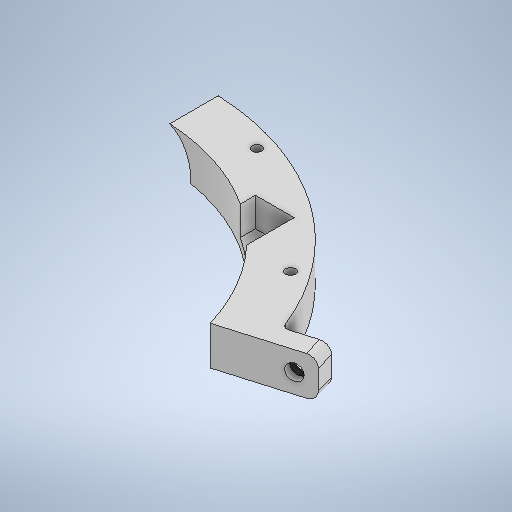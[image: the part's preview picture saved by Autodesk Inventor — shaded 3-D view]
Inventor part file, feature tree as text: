
AUTODESK INVENTOR PART (.ipt)
format: ipt  version: 2025 (Build 290162000, 162)  size: 354,816 bytes
history: native  units: in
note: dims shown in document units (in); Inventor stores cm internally (conversion verified against a paired STEP export)
features: sketch x10, extrude x7, hole x2, fillet x1, projected_geometry x1
ambient origin geometry x8: Origin, YZ Plane, XZ Plane, XY Plane, X Axis, Y Axis, Z Axis, Center Point
bodies: Solid1 (feature_tree)
feature tree (21):
  extrude  "Extrusion1"  Depth=8.6614in
  extrude  "Extrusion2"  Depth=1.4173in
  hole  "Hole1"  [1 undecoded]
  extrude  "Extrusion3"  Depth=0.1575in TaperAngle=360.0deg
  extrude  "Extrusion7"  Depth=0.1575in TaperAngle=0.0deg
  extrude  "Extrusion8"  Depth=2.7559in
  extrude  "Extrusion9"  Depth=0.7874in
  extrude  "Extrusion10"  TaperAngle=0.0deg  [1 undecoded]
  fillet  "Fillet1"  [1 undecoded]
  hole  "Hole2"  [1 undecoded]
  sketch  "Sketch1"  dims[d0=10.6299in d1=8.6614in]
  sketch  "Sketch2"  dims[d5=0.0in d6=0.0in d7=10.0394in]
  sketch  "Sketch3"  dims[d8=0.1575in d9=3.937in d11=360.0deg]
  sketch  "Sketch Circular Pattern1"  dims[d2=1.8504in d3=0.0in d4=1.4173in]
  sketch  "Sketch4"  dims[d13=0.1969in d14=0.3937in d15=0.1575in d16=0.0787in d17=90.0deg d18=0.5591in d19=0.8108in d20=1.063in d21=0.0in]
  sketch  "Sketch7"  dims[d38=0.1181in d39=2.7559in]
  sketch  "Sketch8"  dims[d40=0.7874in d41=7.874in]
  sketch  "Sketch9"  dims[d42=0.5906in d43=0.0in d44=0.0in d45=0.0in d46=0.0in d47=0.0in]
  projected_geometry  "Projected Loop1"
  sketch  "Sketch10"  dims[d48=0.8858in d49=0.7874in]
  sketch  "Sketch11"  dims[d50=0.7874in d51=0.3937in d52=0.0in d53=0.1969in d54=0.0984in d55=0.3937in d56=0.3937in d57=0.3228in d58=0.2362in d59=0.5197in d60=0.2362in d61=90.0deg d62=0.315in d63=0.8108in d30=0.0197in d31=0.0344in d32=0.0197in d33=0.0344in]
note: 4 required parameter values undecoded (feature->parameter linkage not recoverable at this tier; creation-order binding heuristic only, values carry confidence <= 0.55)
